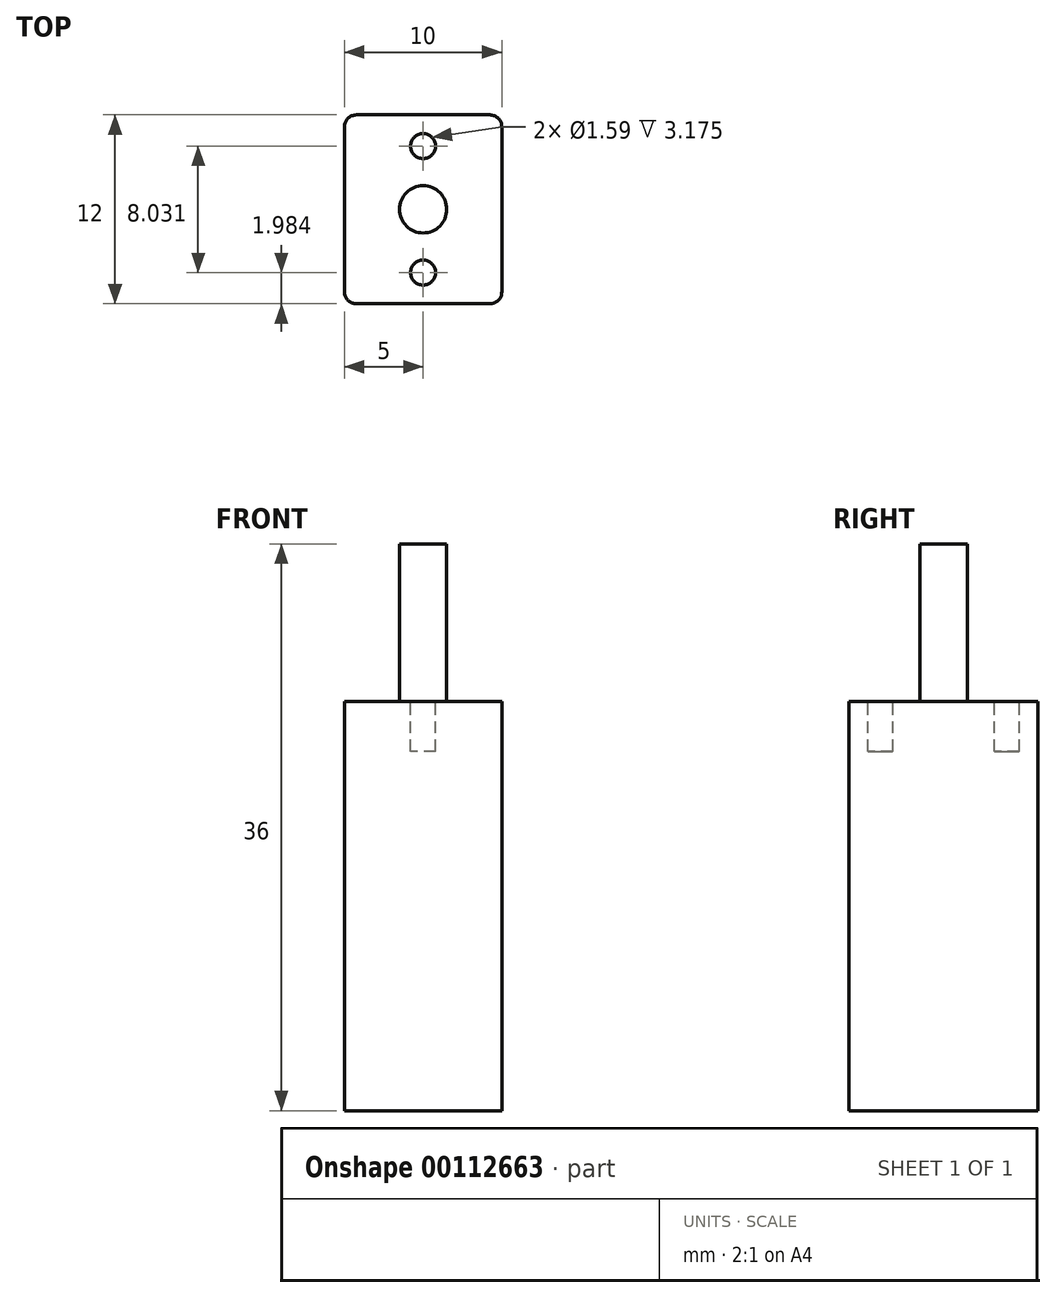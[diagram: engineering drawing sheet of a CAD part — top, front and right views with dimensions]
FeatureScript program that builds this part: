
annotation { "Feature Type Name" : "Feature", "Feature Type Description" : "" }
export const myFeature = defineFeature(function(context is Context, id is Id, definition is map)
    precondition{}
    {
        {
            var Q0;
            Q0=qCreatedBy(makeId("Top.planeOp"),FACE);
            var sketch = newSketch(context, id + "F0", { "sketchPlane" : qUnion([Q0])});
            skLineSegment(sketch, "E0.bottom", {"start": v(5, -6) * mm, "end": v(-5, -6) * mm});
            skLineSegment(sketch, "E0.top", {"start": v(5, 6) * mm, "end": v(-5, 6) * mm});
            skLineSegment(sketch, "E0.left", {"start": v(5, -6) * mm, "end": v(5, 6) * mm});
            skLineSegment(sketch, "E0.right", {"start": v(-5, -6) * mm, "end": v(-5, 6) * mm});
            skPoint(sketch, "E0.middle", {"position": v(0, 0) * mm});
            skSolve(sketch);
        }
        {
            var Q0;
            Q0 = qSketchRegion(id + "F0", true);
            extrude(context, id + "F1", {"entities" : qUnion([Q0]), "depth" : 26 * mm});
        }
        {
            var Q0;
            Q0=makeQuery(id+"F1.opExtrude","SWEPT_EDGE",EDGE,{"disambiguationData":[OSD([sQuery(id+"F0.wireOp",EDGE,"E0.bottom"),sQuery(id+"F0.wireOp",EDGE,"E0.right")])]});
            var Q1;
            Q1=makeQuery(id+"F1.opExtrude","SWEPT_EDGE",EDGE,{"disambiguationData":[OSD([sQuery(id+"F0.wireOp",EDGE,"E0.top"),sQuery(id+"F0.wireOp",EDGE,"E0.right")])]});
            var Q2;
            Q2=makeQuery(id+"F1.opExtrude","SWEPT_EDGE",EDGE,{"disambiguationData":[OSD([sQuery(id+"F0.wireOp",EDGE,"E0.bottom"),sQuery(id+"F0.wireOp",EDGE,"E0.left")])]});
            var Q3;
            Q3=makeQuery(id+"F1.opExtrude","SWEPT_EDGE",EDGE,{"disambiguationData":[OSD([sQuery(id+"F0.wireOp",EDGE,"E0.top"),sQuery(id+"F0.wireOp",EDGE,"E0.left")])]});
            fillet(context, id + "F2", {"entities" : qUnion([Q0, Q1, Q2, Q3]), "radius" : 0.76 * mm, "tangentPropagation" : true, "allowEdgeOverflow" : false});
        }
        {
            var Q0;
            Q0=makeQuery(id+"F1.opExtrude","CAP_FACE",FACE,{"disambiguationData":[OSD([sQuery(id+"F0.wireOp",EDGE,"E0.bottom"),sQuery(id+"F0.wireOp",EDGE,"E0.top"),sQuery(id+"F0.wireOp",EDGE,"E0.left"),sQuery(id+"F0.wireOp",EDGE,"E0.right")])],"isStart":false});
            var sketch = newSketch(context, id + "F3", { "sketchPlane" : qUnion([Q0])});
            skLineSegment(sketch, "E1", {"start": v(0, -6) * mm, "end": v(0, 6) * mm, "construction": true});
            skCircle(sketch, "E2", {"center": v(0, 0) * mm, "radius": 1.5 * mm});
            skSolve(sketch);
        }
        {
            var Q0;
            Q0 = qSketchRegion(id + "F3", true);
            extrude(context, id + "F4", {"entities" : qUnion([Q0]), "operationType" : NewBodyOperationType.ADD, "depth" : 10 * mm});
        }
        {
            var Q0;
            Q0=makeQuery(id+"F1.opExtrude","CAP_FACE",FACE,{"disambiguationData":[OSD([sQuery(id+"F0.wireOp",EDGE,"E0.bottom"),sQuery(id+"F0.wireOp",EDGE,"E0.top"),sQuery(id+"F0.wireOp",EDGE,"E0.left"),sQuery(id+"F0.wireOp",EDGE,"E0.right")])],"isStart":false});
            var sketch = newSketch(context, id + "F5", { "sketchPlane" : qUnion([Q0])});
            skLineSegment(sketch, "E3", {"start": v(0, 6) * mm, "end": v(0, 4.02) * mm, "construction": true});
            skLineSegment(sketch, "E4", {"start": v(0, -6) * mm, "end": v(0, -4.02) * mm, "construction": true});
            skCircle(sketch, "E5", {"center": v(0, 4.02) * mm, "radius": 0.8 * mm});
            skCircle(sketch, "E6", {"center": v(0, -4.02) * mm, "radius": 0.8 * mm});
            skSolve(sketch);
        }
        {
            var Q0;
            Q0 = qSketchRegion(id + "F5", true);
            extrude(context, id + "F6", {"entities" : qUnion([Q0]), "operationType" : NewBodyOperationType.REMOVE, "oppositeDirection" : true, "depth" : 3.17 * mm});
        }
    });
